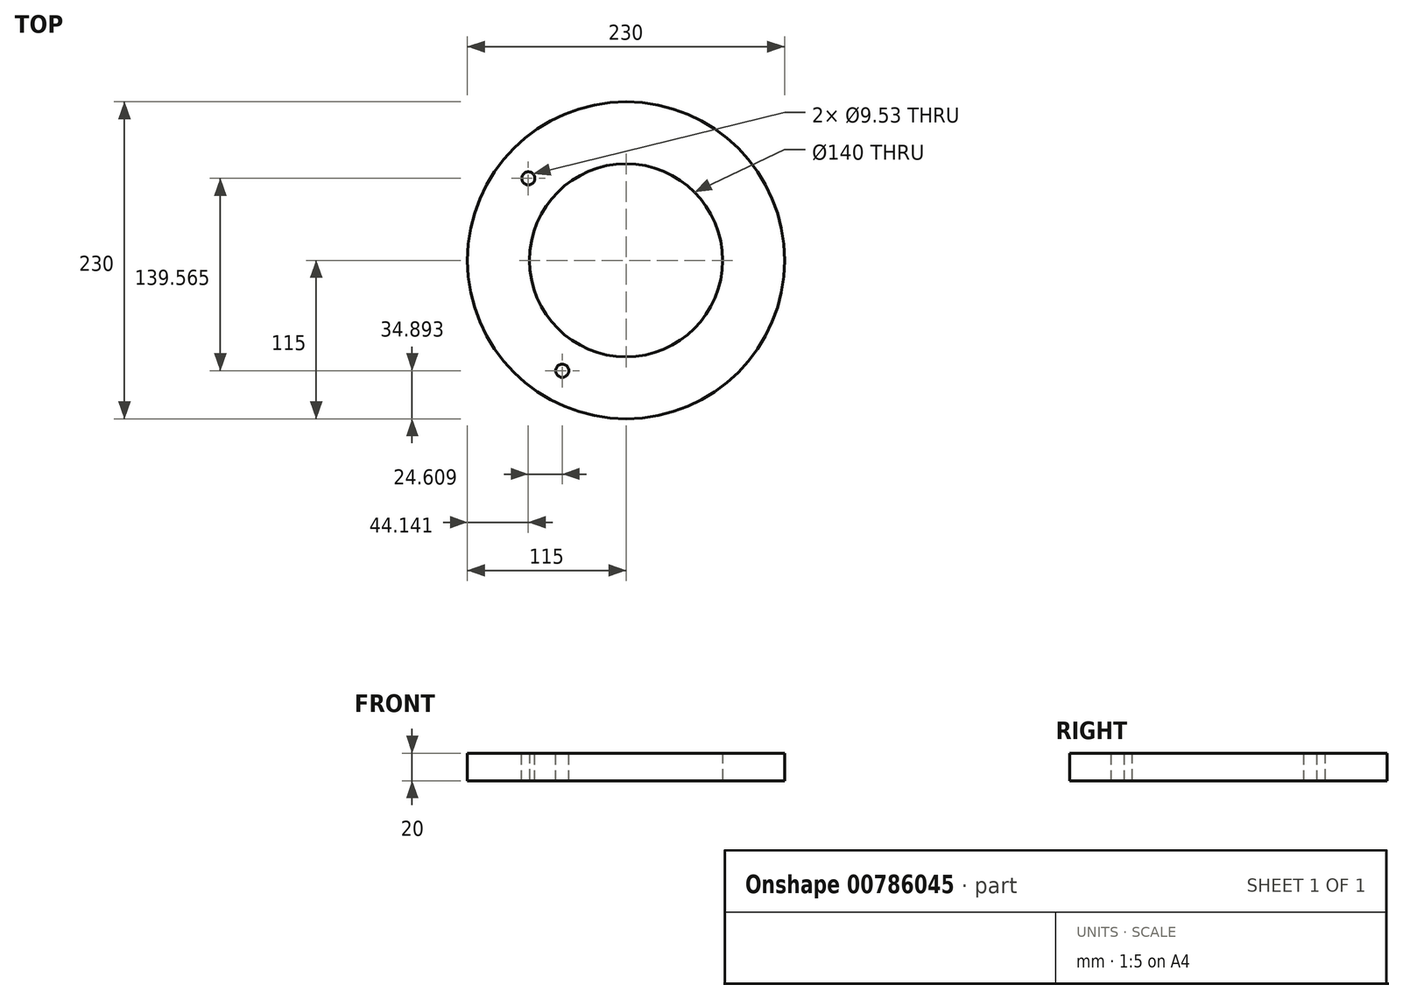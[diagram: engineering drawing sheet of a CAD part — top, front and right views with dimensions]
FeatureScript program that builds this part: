
annotation { "Feature Type Name" : "Feature", "Feature Type Description" : "" }
export const myFeature = defineFeature(function(context is Context, id is Id, definition is map)
    precondition{}
    {
        {
            var Q0;
            Q0=qCreatedBy(makeId("Top.planeOp"),FACE);
            var sketch = newSketch(context, id + "F0", { "sketchPlane" : qUnion([Q0])});
            skCircle(sketch, "E0", {"center": v(0, 0) * mm, "radius": 115 * mm});
            skCircle(sketch, "E1", {"center": v(0, 0) * mm, "radius": 70 * mm});
            skSolve(sketch);
        }
        {
            var Q0;
            Q0=qSketchRegion(id+"F0",true);
            extrude(context, id + "F1", {"entities" : qUnion([Q0]), "depth" : 20 * mm});
        }
        {
            var Q0;
            Q0=makeQuery(id+"F1.opExtrude","CAP_FACE",FACE,{"disambiguationData":[OSD([sQuery(id+"F0.wireOp",EDGE,"E0"),sQuery(id+"F0.wireOp",EDGE,"E1")])],"isStart":false});
            var sketch = newSketch(context, id + "F2", { "sketchPlane" : qUnion([Q0])});
            skCircle(sketch, "E2", {"center": v(0, 0) * mm, "radius": 92.5 * mm, "construction": true});
            skCircle(sketch, "E3", {"center": v(-70.86, 59.46) * mm, "radius": 4.76 * mm});
            skCircle(sketch, "E4", {"center": v(-46.25, -80.1) * mm, "radius": 4.76 * mm});
            skLineSegment(sketch, "E5", {"start": v(-70.86, 59.46) * mm, "end": v(0, 0) * mm, "construction": true});
            skLineSegment(sketch, "E6", {"start": v(0, 0) * mm, "end": v(-46.25, -80.1) * mm, "construction": true});
            skLineSegment(sketch, "E7", {"start": v(0, 0) * mm, "end": v(-92.5, 0) * mm, "construction": true});
            skLineSegment(sketch, "E8", {"start": v(0, 92.5) * mm, "end": v(0, -92.5) * mm, "construction": true});
            skCircle(sketch, "E9", {"center": v(92.5, 0) * mm, "radius": 4.76 * mm, "construction": true});
            skSolve(sketch);
        }
        {
            var Q0;
            Q0=qSketchRegion(id+"F2",true);
            extrude(context, id + "F3", {"entities" : qUnion([Q0]), "operationType" : NewBodyOperationType.REMOVE, "oppositeDirection" : true, "depth" : 25 * mm, "offsetDistance" : 25 * mm});
        }
    });
